# Revit family: Worksurface-Teknion-HNBWTN_Navigate_120-R2016
name_source: partatom
category: Furniture
revit_build: Autodesk Revit Architecture 2016 (Build: 20190507_1515(x64)
units: mm (PartAtom-declared; Revit-internal decimal feet)

## family parameters
Always vertical = Yes
Cut with Voids When Loaded = No
OmniClass Number = 23.40.20.00
OmniClass Title = General Furniture and Specialties
Room Calculation Point = No
Shared = No
Work Plane-Based = No

## types (4) — shared parameters
Available Depths = 22, 23, 28, 29 inches.
Manufacturer = Teknion
Manufacturer Fax = 416.661.4586
Part Number = HNBWTN
Product Documentation Link = https://www.teknion.com
Product Line = Navigate Height-Adjustable Bench
Product Page URL = https://www.teknion.com
Series = Navigate Height-Adjustable Bench
URL = www.teknion.com
Warranty = http://www.teknion.com

## per-type parameters (varying)
| type | Actual Depth | Depth | Description | Model |
| 28" Depth | 27.5 " | 28 " | Navigate 120 Worksurface, 28" Depth | HNBWTN28___ |
| 29" Depth | 28.5 " | 29 " | Navigate 120 Worksurface, 29" Depth | HNBWTN29___ |
| 23" Depth | 22.5 " | 23 " | Navigate 120 Worksurface, 23" Depth | HNBWTN23___ |
| 22" Depth | 21.5 " | 22 " | Navigate 120 Worksurface, 22" Depth | HNBWTN22___ |

## geometry (parser evidence)
native form markers: Sweep x1
no freeform markers — native parametric forms only
